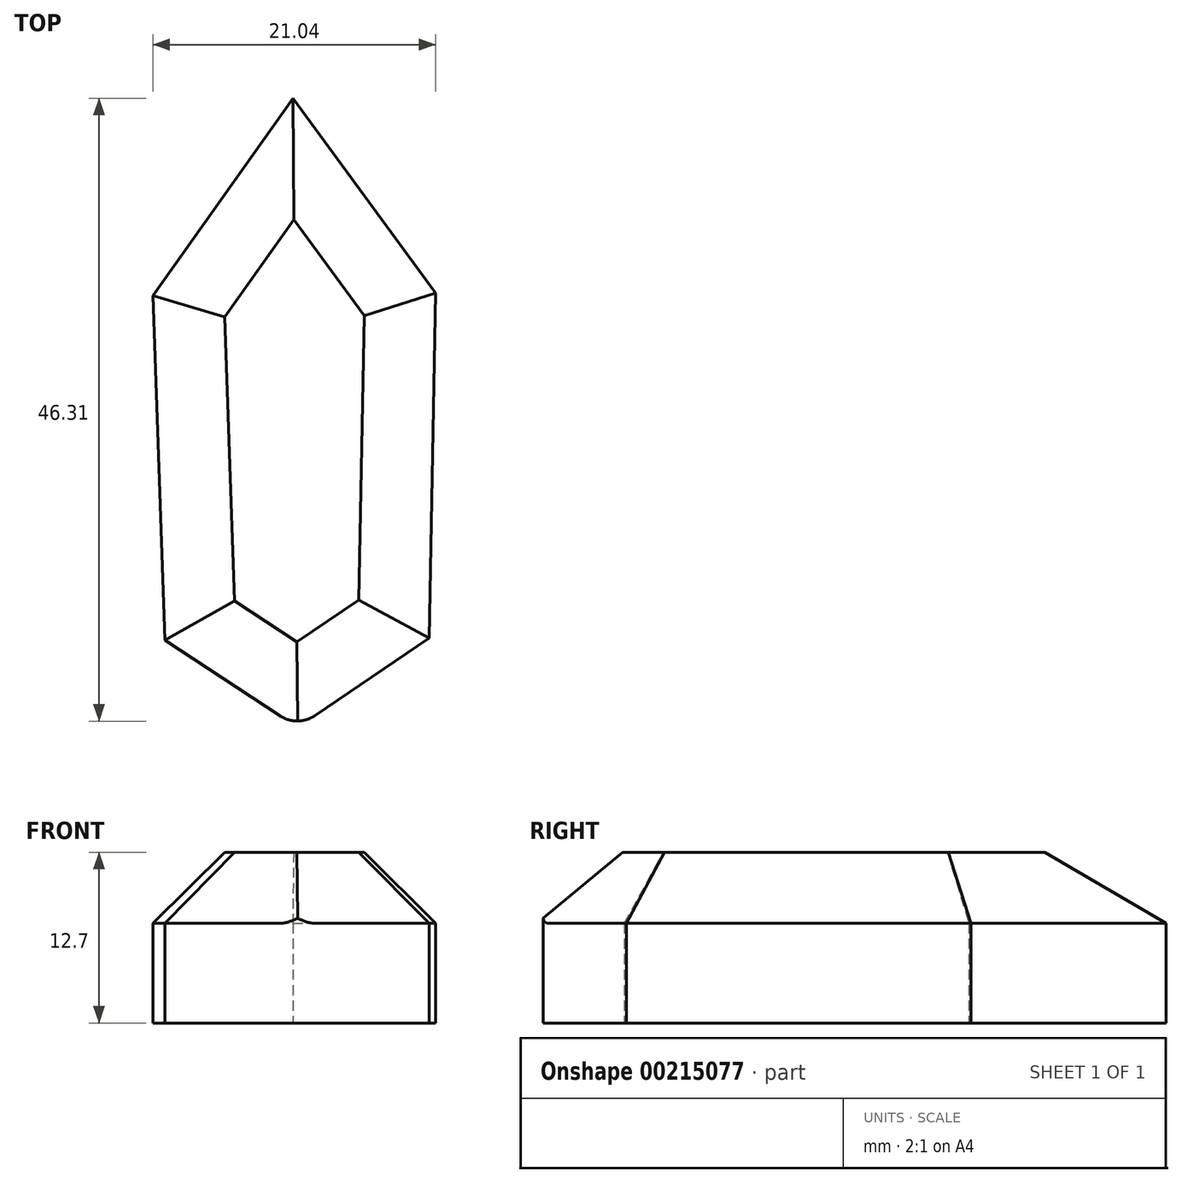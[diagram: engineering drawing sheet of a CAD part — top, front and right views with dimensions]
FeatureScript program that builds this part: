
annotation { "Feature Type Name" : "Feature", "Feature Type Description" : "" }
export const myFeature = defineFeature(function(context is Context, id is Id, definition is map)
    precondition{}
    {
        {
            var Q0;
            Q0=qCreatedBy(makeId("Top.planeOp"),FACE);
            var sketch = newSketch(context, id + "F1", { "sketchPlane" : qUnion([Q0])});
            skLineSegment(sketch, "E0", {"start": v(0, 26.37) * mm, "end": v(10.63, 11.88) * mm});
            skLineSegment(sketch, "E1", {"start": v(10.63, 11.88) * mm, "end": v(10.13, -13.76) * mm});
            skLineSegment(sketch, "E2", {"start": v(10.13, -13.76) * mm, "end": v(0.36, -20.4) * mm});
            skLineSegment(sketch, "E3", {"start": v(0.36, -20.4) * mm, "end": v(0, 26.37) * mm});
            skLineSegment(sketch, "E4.MirrorCS", {"start": v(0, 26.37) * mm, "end": v(-10.4, 11.71) * mm});
            skLineSegment(sketch, "E5.MirrorCS", {"start": v(-9.51, -13.9) * mm, "end": v(0.36, -20.4) * mm});
            skLineSegment(sketch, "E6.MirrorCS", {"start": v(-10.4, 11.71) * mm, "end": v(-9.51, -13.9) * mm});
            skSolve(sketch);
        }
        {
            var Q0;
            Q0=makeQuery(id+"F1.imprint","IMPRINT",FACE,{"disambiguationData":[TD([[makeQuery(id+"F1.imprint","IMPRINT",EDGE,{"derivedFrom":sQuery(id+"F1.wireOp",EDGE,"E0")}),-1.0]])]});
            var Q1;
            Q1=makeQuery(id+"F1.imprint","IMPRINT",FACE,{"disambiguationData":[TD([[makeQuery(id+"F1.imprint","IMPRINT",EDGE,{"derivedFrom":sQuery(id+"F1.wireOp",EDGE,"E4.MirrorCS")}),1.0]])]});
            extrude(context, id + "F2", {"entities" : qUnion([Q0, Q1]), "depth" : 12.7 * mm});
        }
        {
            var Q0;
            Q0=makeQuery(id+"F2.opExtrude","CAP_EDGE",EDGE,{"disambiguationData":[OSD([sQuery(id+"F1.wireOp",EDGE,"E6.MirrorCS")])],"isStart":false});
            var Q1;
            Q1=makeQuery(id+"F2.opExtrude","CAP_EDGE",EDGE,{"disambiguationData":[OSD([sQuery(id+"F1.wireOp",EDGE,"E5.MirrorCS")])],"isStart":false});
            var Q2;
            Q2=makeQuery(id+"F2.opExtrude","CAP_EDGE",EDGE,{"disambiguationData":[OSD([sQuery(id+"F1.wireOp",EDGE,"E2")])],"isStart":false});
            var Q3;
            Q3=makeQuery(id+"F2.opExtrude","CAP_EDGE",EDGE,{"disambiguationData":[OSD([sQuery(id+"F1.wireOp",EDGE,"E1")])],"isStart":false});
            var Q4;
            Q4=makeQuery(id+"F2.opExtrude","CAP_EDGE",EDGE,{"disambiguationData":[OSD([sQuery(id+"F1.wireOp",EDGE,"E0")])],"isStart":false});
            var Q5;
            Q5=makeQuery(id+"F2.opExtrude","CAP_EDGE",EDGE,{"disambiguationData":[OSD([sQuery(id+"F1.wireOp",EDGE,"E4.MirrorCS")])],"isStart":false});
            chamfer(context, id + "F3", {"entities" : qUnion([Q0, Q1, Q2, Q3, Q4, Q5]), "width" : 5.28 * mm, "tangentPropagation" : true});
        }
        {
            var Q0;
            Q0=makeQuery(id+"F2.opExtrude","SWEPT_EDGE",EDGE,{"disambiguationData":[OSD([sQuery(id+"F1.wireOp",EDGE,"E2"),sQuery(id+"F1.wireOp",EDGE,"E5.MirrorCS"),sQuery(id+"F1.wireOp",EDGE,"E3")])]});
            fillet(context, id + "F0", {"entities" : qUnion([Q0]), "radius" : 2.3 * mm, "tangentPropagation" : true, "allowEdgeOverflow" : false});
        }
    });
